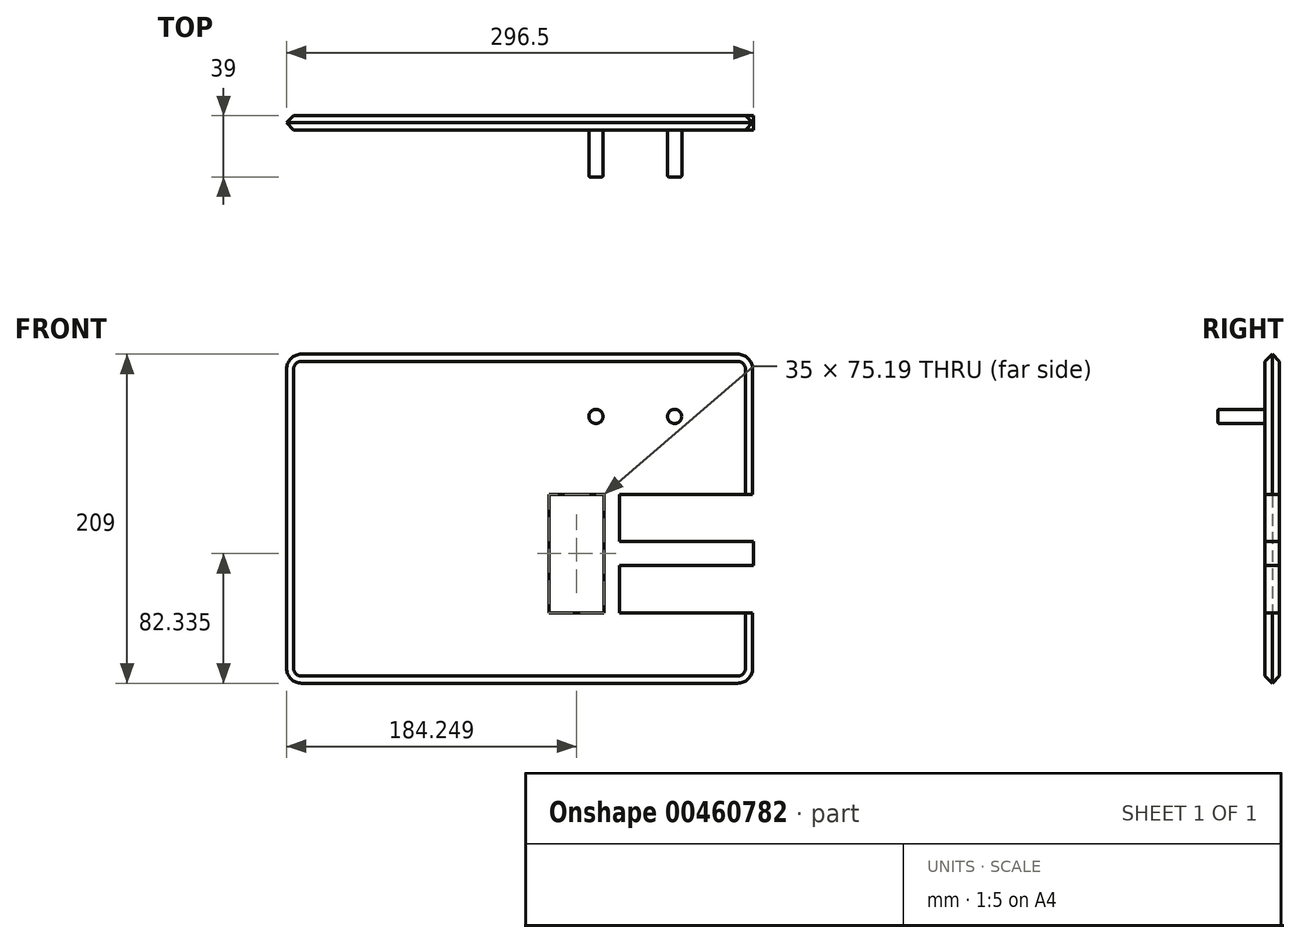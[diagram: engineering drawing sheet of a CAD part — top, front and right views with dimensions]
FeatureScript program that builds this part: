
annotation { "Feature Type Name" : "Feature", "Feature Type Description" : "" }
export const myFeature = defineFeature(function(context is Context, id is Id, definition is map)
    precondition{}
    {
        {
            var Q0;
            Q0=qCreatedBy(makeId("Front.planeOp"),FACE);
            var sketch = newSketch(context, id + "F0", { "sketchPlane" : qUnion([Q0])});
            skLineSegment(sketch, "E0.bottom", {"start": v(-145.07, -4.13) * mm, "end": v(131.93, -4.13) * mm});
            skLineSegment(sketch, "E0.top", {"start": v(-145.07, -214.13) * mm, "end": v(131.93, -214.13) * mm});
            skLineSegment(sketch, "E0.left", {"start": v(-155.07, -14.13) * mm, "end": v(-155.07, -204.13) * mm});
            skLineSegment(sketch, "E0.right", {"start": v(141.93, -14.13) * mm, "end": v(141.93, -204.13) * mm});
            skPoint(sketch, "E1.visualSharp", {"position": v(-155.07, -4.13) * mm});
            skArc(sketch, "E1.filletArc", {"start": v(-145.07, -4.13) * mm, "mid": v(-152.14, -7.06) * mm, "end": v(-155.07, -14.13) * mm});
            skPoint(sketch, "E2.visualSharp", {"position": v(141.93, -214.13) * mm});
            skArc(sketch, "E2.filletArc", {"start": v(131.93, -214.13) * mm, "mid": v(139, -211.2) * mm, "end": v(141.93, -204.13) * mm});
            skPoint(sketch, "E3.visualSharp", {"position": v(141.93, -4.13) * mm});
            skArc(sketch, "E3.filletArc", {"start": v(141.93, -14.13) * mm, "mid": v(139, -7.06) * mm, "end": v(131.93, -4.13) * mm});
            skPoint(sketch, "E4.visualSharp", {"position": v(-155.07, -214.13) * mm});
            skArc(sketch, "E4.filletArc", {"start": v(-155.07, -204.13) * mm, "mid": v(-152.14, -211.2) * mm, "end": v(-145.07, -214.13) * mm});
            skSolve(sketch);
        }
        {
            var Q0;
            Q0=makeQuery(id+"F0.imprint","IMPRINT",FACE,{"disambiguationData":[TD([[makeQuery(id+"F0.imprint","IMPRINT",EDGE,{"derivedFrom":sQuery(id+"F0.wireOp",EDGE,"E0.bottom")}),-1.0]])]});
            extrude(context, id + "F1", {"entities" : qUnion([Q0]), "depth" : 9 * mm});
        }
        {
            var Q0;
            Q0=makeQuery(id+"F1.opExtrude","CAP_FACE",FACE,{"disambiguationData":[OSD([sQuery(id+"F0.wireOp",EDGE,"E0.bottom"),sQuery(id+"F0.wireOp",EDGE,"E0.top"),sQuery(id+"F0.wireOp",EDGE,"E0.left"),sQuery(id+"F0.wireOp",EDGE,"E0.right"),sQuery(id+"F0.wireOp",EDGE,"E1.filletArc"),sQuery(id+"F0.wireOp",EDGE,"E2.filletArc"),sQuery(id+"F0.wireOp",EDGE,"E3.filletArc"),sQuery(id+"F0.wireOp",EDGE,"E4.filletArc")])],"isStart":false});
            var sketch = newSketch(context, id + "F2", { "sketchPlane" : qUnion([Q0])});
            skCircle(sketch, "E5", {"center": v(41.93, -44.13) * mm, "radius": 4.5 * mm});
            skCircle(sketch, "E6", {"center": v(91.93, -44.13) * mm, "radius": 4.5 * mm});
            skSolve(sketch);
        }
        {
            var Q0;
            Q0 = qSketchRegion(id + "F2", true);
            extrude(context, id + "F3", {"entities" : qUnion([Q0]), "operationType" : NewBodyOperationType.ADD, "depth" : 30 * mm});
        }
        {
            var Q0;
            Q0=makeQuery(id+"F1.opExtrude","CAP_FACE",FACE,{"disambiguationData":[OSD([sQuery(id+"F0.wireOp",EDGE,"E0.bottom"),sQuery(id+"F0.wireOp",EDGE,"E0.top"),sQuery(id+"F0.wireOp",EDGE,"E0.left"),sQuery(id+"F0.wireOp",EDGE,"E0.right"),sQuery(id+"F0.wireOp",EDGE,"E1.filletArc"),sQuery(id+"F0.wireOp",EDGE,"E2.filletArc"),sQuery(id+"F0.wireOp",EDGE,"E3.filletArc"),sQuery(id+"F0.wireOp",EDGE,"E4.filletArc")])],"isStart":false});
            var sketch = newSketch(context, id + "F4", { "sketchPlane" : qUnion([Q0])});
            skLineSegment(sketch, "E7.bottom", {"start": v(141.93, -93.7) * mm, "end": v(56.93, -93.7) * mm});
            skLineSegment(sketch, "E7.top", {"start": v(141.93, -123.7) * mm, "end": v(56.93, -123.7) * mm});
            skLineSegment(sketch, "E7.left", {"start": v(141.93, -93.7) * mm, "end": v(141.93, -123.7) * mm});
            skLineSegment(sketch, "E7.right", {"start": v(56.93, -93.7) * mm, "end": v(56.93, -123.7) * mm});
            skSolve(sketch);
        }
        {
            var Q0;
            Q0=makeQuery(id+"F4.imprint","IMPRINT",FACE,{"disambiguationData":[TD([[makeQuery(id+"F4.imprint","IMPRINT",EDGE,{"derivedFrom":sQuery(id+"F4.wireOp",EDGE,"E7.bottom")}),1.0]])]});
            extrude(context, id + "F5", {"entities" : qUnion([Q0]), "operationType" : NewBodyOperationType.REMOVE, "oppositeDirection" : true, "depth" : 25 * mm});
        }
        {
            var Q0;
            Q0=makeQuery(id+"F1.opExtrude","CAP_FACE",FACE,{"disambiguationData":[OSD([sQuery(id+"F0.wireOp",EDGE,"E0.bottom"),sQuery(id+"F0.wireOp",EDGE,"E0.top"),sQuery(id+"F0.wireOp",EDGE,"E0.left"),sQuery(id+"F0.wireOp",EDGE,"E0.right"),sQuery(id+"F0.wireOp",EDGE,"E1.filletArc"),sQuery(id+"F0.wireOp",EDGE,"E2.filletArc"),sQuery(id+"F0.wireOp",EDGE,"E3.filletArc"),sQuery(id+"F0.wireOp",EDGE,"E4.filletArc")])],"isStart":false});
            var sketch = newSketch(context, id + "F6", { "sketchPlane" : qUnion([Q0])});
            skLineSegment(sketch, "E8.bottom", {"start": v(141.93, -138.9) * mm, "end": v(56.93, -138.9) * mm});
            skLineSegment(sketch, "E8.top", {"start": v(141.93, -168.9) * mm, "end": v(56.93, -168.9) * mm});
            skLineSegment(sketch, "E8.left", {"start": v(141.93, -138.9) * mm, "end": v(141.93, -168.9) * mm});
            skLineSegment(sketch, "E8.right", {"start": v(56.93, -138.9) * mm, "end": v(56.93, -168.9) * mm});
            skSolve(sketch);
        }
        {
            var Q0;
            Q0=makeQuery(id+"F6.imprint","IMPRINT",FACE,{"disambiguationData":[TD([[makeQuery(id+"F6.imprint","IMPRINT",EDGE,{"derivedFrom":sQuery(id+"F6.wireOp",EDGE,"E8.bottom")}),1.0]])]});
            extrude(context, id + "F7", {"entities" : qUnion([Q0]), "operationType" : NewBodyOperationType.REMOVE, "oppositeDirection" : true, "depth" : 25 * mm});
        }
        {
            var Q0;
            Q0=makeQuery(id+"F1.opExtrude","CAP_FACE",FACE,{"disambiguationData":[OSD([sQuery(id+"F0.wireOp",EDGE,"E0.bottom"),sQuery(id+"F0.wireOp",EDGE,"E0.top"),sQuery(id+"F0.wireOp",EDGE,"E0.left"),sQuery(id+"F0.wireOp",EDGE,"E0.right"),sQuery(id+"F0.wireOp",EDGE,"E1.filletArc"),sQuery(id+"F0.wireOp",EDGE,"E2.filletArc"),sQuery(id+"F0.wireOp",EDGE,"E3.filletArc"),sQuery(id+"F0.wireOp",EDGE,"E4.filletArc")])],"isStart":false});
            var sketch = newSketch(context, id + "F8", { "sketchPlane" : qUnion([Q0])});
            skLineSegment(sketch, "E9.bottom", {"start": v(12.18, -93.7) * mm, "end": v(47.18, -93.7) * mm});
            skLineSegment(sketch, "E9.top", {"start": v(12.18, -168.9) * mm, "end": v(47.18, -168.9) * mm});
            skLineSegment(sketch, "E9.left", {"start": v(12.18, -93.7) * mm, "end": v(12.18, -168.9) * mm});
            skLineSegment(sketch, "E9.right", {"start": v(47.18, -93.7) * mm, "end": v(47.18, -168.9) * mm});
            skSolve(sketch);
        }
        {
            var Q0;
            Q0=makeQuery(id+"F3.opExtrude","CAP_EDGE",EDGE,{"disambiguationData":[OSD([sQuery(id+"F2.wireOp",EDGE,"E5")])],"isStart":false});
            var Q1;
            Q1=makeQuery(id+"F3.opExtrude","CAP_EDGE",EDGE,{"disambiguationData":[OSD([sQuery(id+"F2.wireOp",EDGE,"E6")])],"isStart":false});
            fillet(context, id + "F9", {"entities" : qUnion([Q0, Q1]), "radius" : 1 * mm, "tangentPropagation" : true, "allowEdgeOverflow" : false});
        }
        {
            var Q0;
            Q0=makeQuery(id+"F1.opExtrude","CAP_EDGE",EDGE,{"disambiguationData":[OSD([sQuery(id+"F0.wireOp",EDGE,"E0.bottom")])],"isStart":false});
            var Q1;
            Q1=makeQuery(id+"F1.opExtrude","CAP_EDGE",EDGE,{"disambiguationData":[OSD([sQuery(id+"F0.wireOp",EDGE,"E0.bottom")])],"isStart":true});
            chamfer(context, id + "F10", {"entities" : qUnion([Q0, Q1]), "width" : 5 * mm, "tangentPropagation" : true});
        }
        {
            var Q0;
            Q0=makeQuery(id+"F8.imprint","IMPRINT",FACE,{"disambiguationData":[TD([[makeQuery(id+"F8.imprint","IMPRINT",EDGE,{"derivedFrom":sQuery(id+"F8.wireOp",EDGE,"E9.bottom")}),-1.0]])]});
            extrude(context, id + "F11", {"entities" : qUnion([Q0]), "operationType" : NewBodyOperationType.REMOVE, "oppositeDirection" : true, "depth" : 25 * mm});
        }
    });
